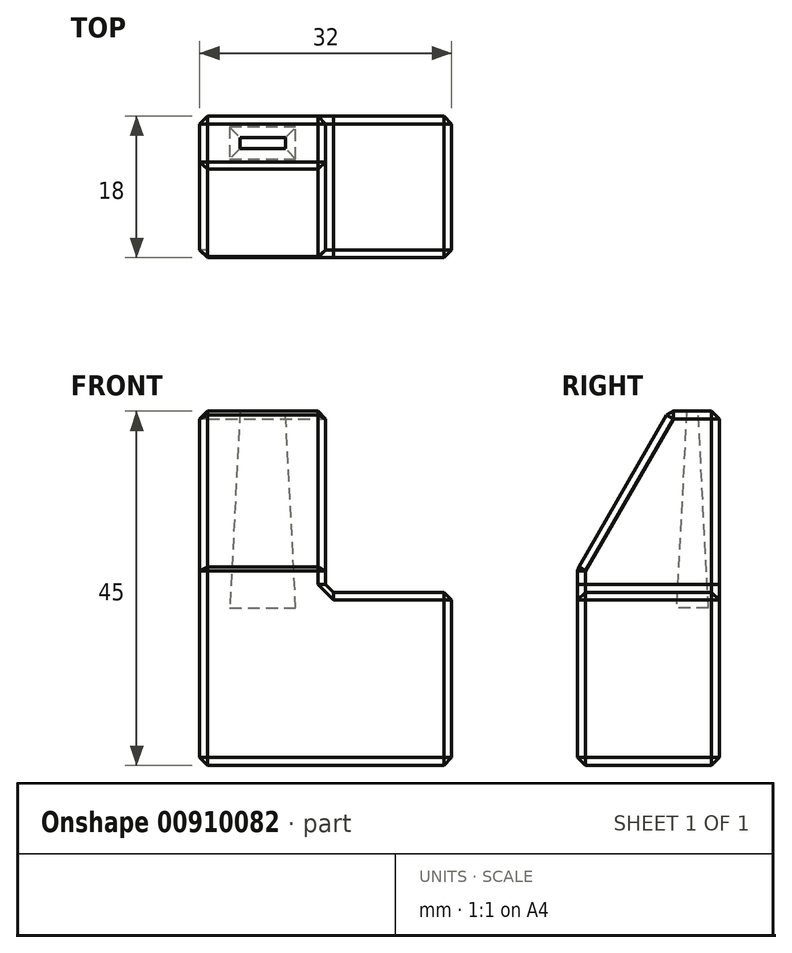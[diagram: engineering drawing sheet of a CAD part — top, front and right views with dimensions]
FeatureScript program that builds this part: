
annotation { "Feature Type Name" : "Feature", "Feature Type Description" : "" }
export const myFeature = defineFeature(function(context is Context, id is Id, definition is map)
    precondition{}
    {
        {
            var Q0;
            Q0=qCreatedBy(makeId("Front.planeOp"),FACE);
            var sketch = newSketch(context, id + "F0", { "sketchPlane" : qUnion([Q0])});
            skLineSegment(sketch, "E0.bottom", {"start": v(12, 7.75) * mm, "end": v(-12, 7.75) * mm, "construction": true});
            skLineSegment(sketch, "E0.top", {"start": v(12, -7.75) * mm, "end": v(-12, -7.75) * mm, "construction": true});
            skLineSegment(sketch, "E0.left", {"start": v(12, 7.75) * mm, "end": v(12, -7.75) * mm, "construction": true});
            skLineSegment(sketch, "E0.right", {"start": v(-12, 7.75) * mm, "end": v(-12, -7.75) * mm, "construction": true});
            skPoint(sketch, "E0.middle", {"position": v(0, 0) * mm});
            skLineSegment(sketch, "E1.bottom", {"start": v(16, 11) * mm, "end": v(0, 11) * mm});
            skLineSegment(sketch, "E1.top", {"start": v(16, -11) * mm, "end": v(-16, -11) * mm});
            skLineSegment(sketch, "E1.left", {"start": v(16, 11) * mm, "end": v(16, -11) * mm});
            skLineSegment(sketch, "E1.right", {"start": v(-16, 11) * mm, "end": v(-16, -11) * mm});
            skLineSegment(sketch, "E2.top", {"start": v(-16, 34) * mm, "end": v(0, 34) * mm});
            skLineSegment(sketch, "E2.left", {"start": v(-16, 11) * mm, "end": v(-16, 34) * mm});
            skLineSegment(sketch, "E2.right", {"start": v(0, 11) * mm, "end": v(0, 34) * mm});
            skSolve(sketch);
        }
        {
            var Q0;
            Q0=makeQuery(id+"F0.imprint","IMPRINT",FACE,{"disambiguationData":[TD([[makeQuery(id+"F0.imprint","IMPRINT",EDGE,{"derivedFrom":sQuery(id+"F0.wireOp",EDGE,"E1.bottom")}),1.0]])]});
            extrude(context, id + "F1", {"entities" : qUnion([Q0]), "depth" : 18 * mm, "offsetDistance" : 25 * mm});
        }
        {
            var Q0;
            Q0=makeQuery(id+"F1.opExtrude","SWEPT_FACE",FACE,{"disambiguationData":[OSD([sQuery(id+"F0.wireOp",EDGE,"E1.right"),sQuery(id+"F0.wireOp",EDGE,"E2.left")])]});
            var sketch = newSketch(context, id + "F2", { "sketchPlane" : qUnion([Q0])});
            skLineSegment(sketch, "E3", {"start": v(6.44, 34) * mm, "end": v(18, 13.98) * mm});
            skLineSegment(sketch, "E4", {"start": v(18, 13.98) * mm, "end": v(18, 34) * mm});
            skLineSegment(sketch, "E5", {"start": v(18, 34) * mm, "end": v(6.44, 34) * mm});
            skSolve(sketch);
        }
        {
            var Q0;
            Q0=makeQuery(id+"F2.imprint","IMPRINT",FACE,{"disambiguationData":[TD([[makeQuery(id+"F2.imprint","IMPRINT",EDGE,{"derivedFrom":sQuery(id+"F2.wireOp",EDGE,"E3")}),1.0]])]});
            extrude(context, id + "F3", {"entities" : qUnion([Q0]), "operationType" : NewBodyOperationType.REMOVE, "oppositeDirection" : true, "depth" : 25 * mm, "offsetDistance" : 25 * mm});
        }
        {
            var Q0;
            Q0=makeQuery(id+"F3.boolean.opBoolean","COPY",FACE,{"derivedFrom":makeQuery(id+"F3.opExtrude","SWEPT_FACE",FACE,{"disambiguationData":[OSD([sQuery(id+"F2.wireOp",EDGE,"E3")])]})});
            var Q1;
            Q1=makeQuery(id+"F1.opExtrude","CAP_FACE",FACE,{"disambiguationData":[OSD([sQuery(id+"F0.wireOp",EDGE,"E1.bottom"),sQuery(id+"F0.wireOp",EDGE,"E1.top"),sQuery(id+"F0.wireOp",EDGE,"E1.left"),sQuery(id+"F0.wireOp",EDGE,"E1.right"),sQuery(id+"F0.wireOp",EDGE,"E2.top"),sQuery(id+"F0.wireOp",EDGE,"E2.left"),sQuery(id+"F0.wireOp",EDGE,"E2.right")])],"isStart":false});
            var Q2;
            Q2=makeQuery(id+"F1.opExtrude","SWEPT_FACE",FACE,{"disambiguationData":[OSD([sQuery(id+"F0.wireOp",EDGE,"E1.right"),sQuery(id+"F0.wireOp",EDGE,"E2.left")])]});
            var Q3;
            Q3=makeQuery(id+"F1.opExtrude","SWEPT_FACE",FACE,{"disambiguationData":[OSD([sQuery(id+"F0.wireOp",EDGE,"E2.top")])]});
            var Q4;
            Q4=makeQuery(id+"F1.opExtrude","SWEPT_FACE",FACE,{"disambiguationData":[OSD([sQuery(id+"F0.wireOp",EDGE,"E2.right")])]});
            var Q5;
            Q5=makeQuery(id+"F1.opExtrude","SWEPT_FACE",FACE,{"disambiguationData":[OSD([sQuery(id+"F0.wireOp",EDGE,"E1.left")])]});
            var Q6;
            Q6=makeQuery(id+"F1.opExtrude","SWEPT_FACE",FACE,{"disambiguationData":[OSD([sQuery(id+"F0.wireOp",EDGE,"E1.top")])]});
            chamfer(context, id + "F4", {"entities" : qUnion([Q0, Q1, Q2, Q3, Q4, Q5, Q6]), "width" : 1 * mm, "tangentPropagation" : true});
        }
        {
            var Q0;
            Q0=makeQuery(id+"F1.opExtrude","SWEPT_FACE",FACE,{"disambiguationData":[OSD([sQuery(id+"F0.wireOp",EDGE,"E2.top")])]});
            var sketch = newSketch(context, id + "F5", { "sketchPlane" : qUnion([Q0])});
            skLineSegment(sketch, "E6.bottom", {"start": v(-10.88, -4.16) * mm, "end": v(-5.12, -4.16) * mm});
            skLineSegment(sketch, "E6.top", {"start": v(-10.88, -2.7) * mm, "end": v(-5.12, -2.7) * mm});
            skLineSegment(sketch, "E6.left", {"start": v(-10.88, -4.16) * mm, "end": v(-10.88, -2.7) * mm});
            skLineSegment(sketch, "E6.right", {"start": v(-5.12, -4.16) * mm, "end": v(-5.12, -2.7) * mm});
            skPoint(sketch, "E6.middle", {"position": v(-8, -3.43) * mm});
            skPoint(sketch, "E6.middle.positionSnap0", {"position": v(-8, -5.86) * mm});
            skPoint(sketch, "E6.middle.positionSnap1", {"position": v(-15, -3.43) * mm});
            skPoint(sketch, "E6.centerSnap0", {"position": v(-8, -5.86) * mm});
            skPoint(sketch, "E6.centerSnap1", {"position": v(-15, -3.43) * mm});
            skSolve(sketch);
        }
        {
            var Q0;
            Q0 = qSketchRegion(id + "F5", true);
            extrude(context, id + "F6", {"entities" : qUnion([Q0]), "operationType" : NewBodyOperationType.REMOVE, "oppositeDirection" : true, "depth" : 25 * mm, "offsetDistance" : 25 * mm, "hasDraft" : true, "draftAngle" : 3 * degree});
        }
    });
